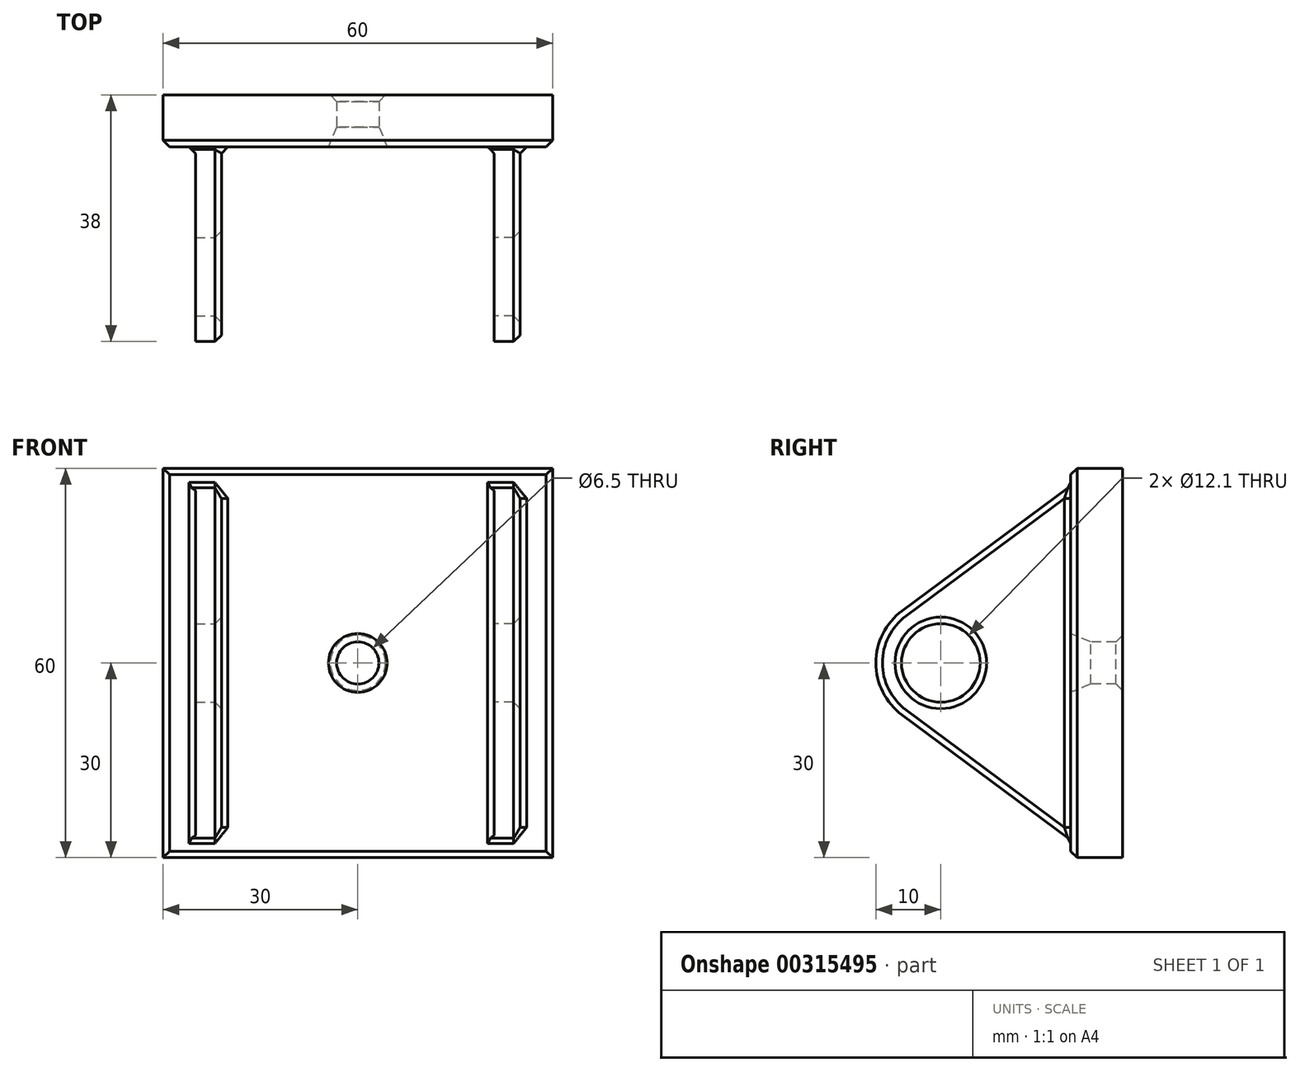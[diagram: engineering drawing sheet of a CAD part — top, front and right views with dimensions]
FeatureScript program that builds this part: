
annotation { "Feature Type Name" : "Feature", "Feature Type Description" : "" }
export const myFeature = defineFeature(function(context is Context, id is Id, definition is map)
    precondition{}
    {
        {
            var Q0;
            Q0=qCreatedBy(makeId("Front.planeOp"),FACE);
            var sketch = newSketch(context, id + "F0", { "sketchPlane" : qUnion([Q0])});
            skLineSegment(sketch, "E0.bottom", {"start": v(30, 30) * mm, "end": v(-30, 30) * mm});
            skLineSegment(sketch, "E0.top", {"start": v(30, -30) * mm, "end": v(-30, -30) * mm});
            skLineSegment(sketch, "E0.left", {"start": v(30, 30) * mm, "end": v(30, -30) * mm});
            skLineSegment(sketch, "E0.right", {"start": v(-30, 30) * mm, "end": v(-30, -30) * mm});
            skCircle(sketch, "E1", {"center": v(0, 0) * mm, "radius": 3.25 * mm});
            skSolve(sketch);
        }
        {
            var Q0;
            Q0=makeQuery(id+"F0.imprint","IMPRINT",FACE,{"disambiguationData":[TD([[makeQuery(id+"F0.imprint","IMPRINT",EDGE,{"derivedFrom":sQuery(id+"F0.wireOp",EDGE,"E0.bottom")}),1.0]])]});
            extrude(context, id + "F1", {"entities" : qUnion([Q0]), "oppositeDirection" : true, "depth" : 8 * mm});
        }
        {
            var Q0;
            Q0=qCreatedBy(makeId("Right.planeOp"),FACE);
            var sketch = newSketch(context, id + "F2", { "sketchPlane" : qUnion([Q0])});
            skLineSegment(sketch, "E2", {"start": v(-20, 15.56) * mm, "end": v(-20, -14.44) * mm, "construction": true});
            skLineSegment(sketch, "E3", {"start": v(-28.89, 0) * mm, "end": v(-9.33, 0) * mm, "construction": true});
            skCircle(sketch, "E4", {"center": v(-20, 0) * mm, "radius": 6.05 * mm});
            skLineSegment(sketch, "E5", {"start": v(0, 27.3) * mm, "end": v(-25.96, 8.03) * mm});
            skLineSegment(sketch, "E6.MirrorCS", {"start": v(0, -27.3) * mm, "end": v(-25.96, -8.03) * mm});
            skArc(sketch, "E7", {"start": v(-25.96, 8.03) * mm, "mid": v(-30, 0) * mm, "end": v(-25.96, -8.03) * mm});
            skLineSegment(sketch, "E8", {"start": v(0, 27.3) * mm, "end": v(0, -27.3) * mm});
            skSolve(sketch);
        }
        {
            var Q0;
            Q0=makeQuery(id+"F2.imprint","IMPRINT",FACE,{"disambiguationData":[TD([[makeQuery(id+"F2.imprint","IMPRINT",EDGE,{"derivedFrom":sQuery(id+"F2.wireOp",EDGE,"E4")}),-1.0]])]});
            extrude(context, id + "F3", {"entities" : qUnion([Q0]), "operationType" : NewBodyOperationType.ADD, "depth" : 25 * mm, "hasSecondDirection" : true, "secondDirectionOppositeDirection" : true, "secondDirectionDepth" : -21 * mm});
        }
        {
            var Q0;
            Q0=makeQuery(id+"F2.imprint","IMPRINT",FACE,{"disambiguationData":[TD([[makeQuery(id+"F2.imprint","IMPRINT",EDGE,{"derivedFrom":sQuery(id+"F2.wireOp",EDGE,"E4")}),-1.0]])]});
            extrude(context, id + "F4", {"entities" : qUnion([Q0]), "operationType" : NewBodyOperationType.ADD, "depth" : -25 * mm, "hasSecondDirection" : true, "secondDirectionOppositeDirection" : true, "secondDirectionDepth" : 21 * mm});
        }
        {
            var Q0;
            Q0=makeQuery(id+"F4.opExtrude","CAP_FACE",FACE,{"disambiguationData":[OSD([sQuery(id+"F2.wireOp",EDGE,"E4"),sQuery(id+"F2.wireOp",EDGE,"E5"),sQuery(id+"F2.wireOp",EDGE,"E6.MirrorCS"),sQuery(id+"F2.wireOp",EDGE,"E7"),sQuery(id+"F2.wireOp",EDGE,"E8")])],"isStart":true});
            var Q1;
            Q1=makeQuery(id+"F3.opExtrude","CAP_FACE",FACE,{"disambiguationData":[OSD([sQuery(id+"F2.wireOp",EDGE,"E4"),sQuery(id+"F2.wireOp",EDGE,"E5"),sQuery(id+"F2.wireOp",EDGE,"E6.MirrorCS"),sQuery(id+"F2.wireOp",EDGE,"E7"),sQuery(id+"F2.wireOp",EDGE,"E8")])],"isStart":false});
            var Q2;
            Q2=makeQuery(id+"F1.opExtrude","CAP_EDGE",EDGE,{"disambiguationData":[OSD([sQuery(id+"F0.wireOp",EDGE,"E1")])],"isStart":true});
            var Q3;
            Q3=makeQuery(id+"F1.opExtrude","CAP_FACE",FACE,{"disambiguationData":[OSD([sQuery(id+"F0.wireOp",EDGE,"E0.bottom"),sQuery(id+"F0.wireOp",EDGE,"E0.top"),sQuery(id+"F0.wireOp",EDGE,"E0.left"),sQuery(id+"F0.wireOp",EDGE,"E0.right"),sQuery(id+"F0.wireOp",EDGE,"E1")])],"isStart":true});
            var Q4;
            Q4=makeQuery(id+"F1.opExtrude","CAP_EDGE",EDGE,{"disambiguationData":[OSD([sQuery(id+"F0.wireOp",EDGE,"E1")])],"isStart":false});
            chamfer(context, id + "F5", {"entities" : qUnion([Q0, Q1, Q2, Q3, Q4]), "width" : 1 * mm, "tangentPropagation" : true});
        }
        {
            var Q0;
            {var subQ0=sQuery(id+"F0.wireOp",EDGE,"E1");Q0=makeQuery(id+"F5.opChamfer","BLEND_EDGE",EDGE,{"blendedFrom":[makeQuery(id+"F1.opExtrude","CAP_EDGE",EDGE,{"disambiguationData":[OSD([subQ0])],"isStart":true}),makeQuery(id+"F1.opExtrude","SWEPT_FACE",FACE,{"disambiguationData":[OSD([subQ0])]})],"blendedInto":[makeQuery(id+"F1.opExtrude","SWEPT_FACE",FACE,{"disambiguationData":[OSD([subQ0])]})]});}
            chamfer(context, id + "F6", {"entities" : qUnion([Q0]), "width" : 5 * mm, "tangentPropagation" : true});
        }
    });
